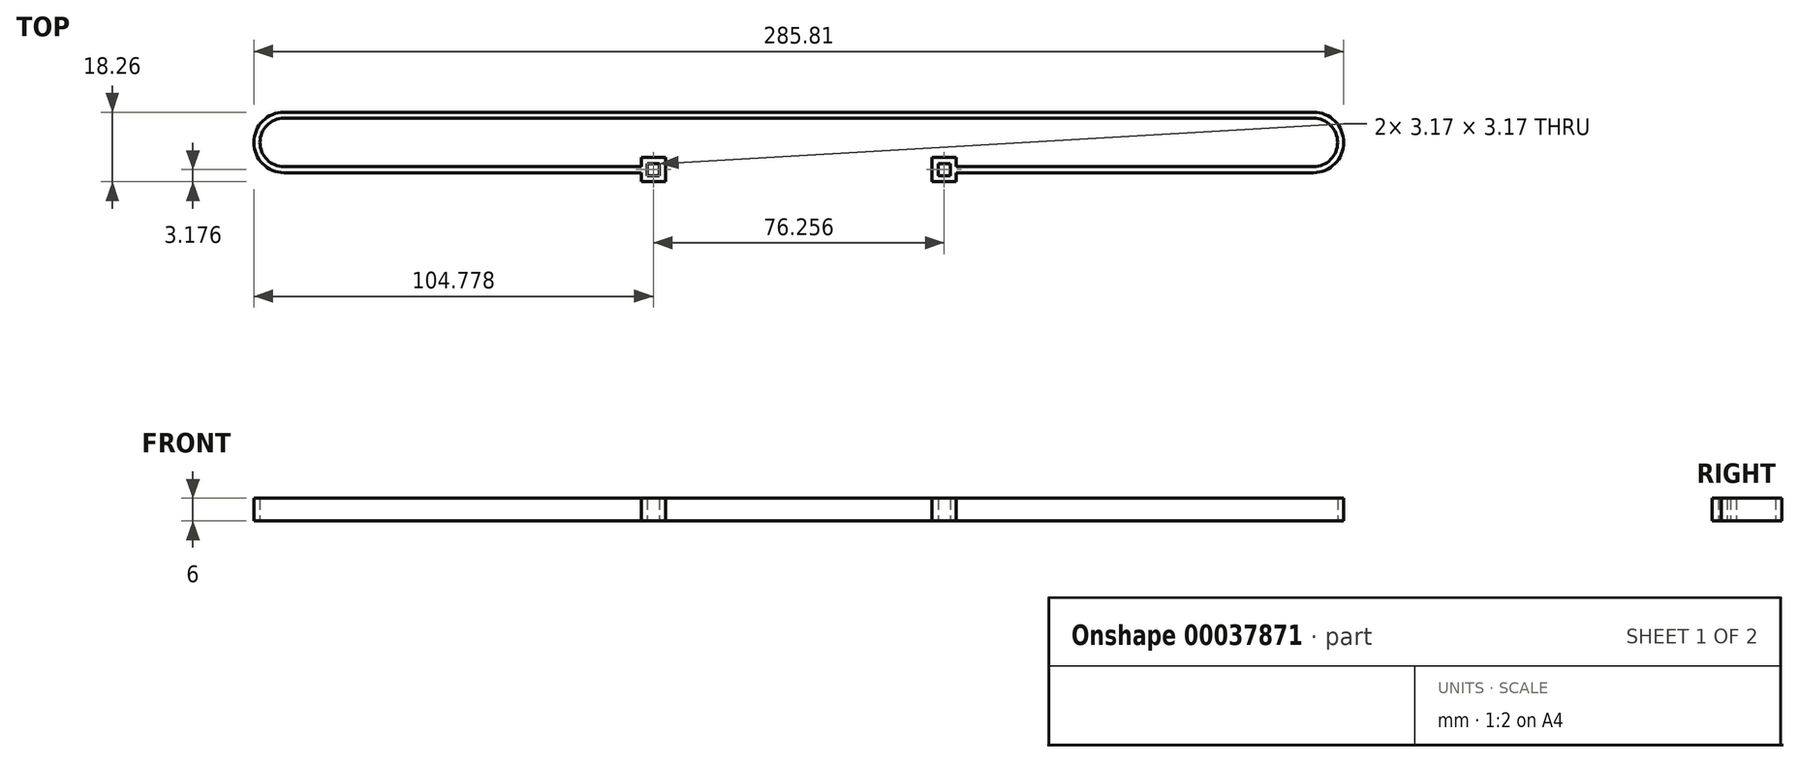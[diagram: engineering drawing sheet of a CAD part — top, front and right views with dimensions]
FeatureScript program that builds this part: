
annotation { "Feature Type Name" : "Feature", "Feature Type Description" : "" }
export const myFeature = defineFeature(function(context is Context, id is Id, definition is map)
    precondition{}
    {
        {
            var Q0;
            Q0=qCreatedBy(makeId("Top.planeOp"),FACE);
            var sketch = newSketch(context, id + "F0", { "sketchPlane" : qUnion([Q0])});
            skLineSegment(sketch, "E0", {"start": v(-672, -278.67) * mm, "end": v(-672, -277.09) * mm, "construction": true});
            skLineSegment(sketch, "E1", {"start": v(-824.4, -300.67) * mm, "end": v(-824.4, -302.26) * mm, "construction": true});
            skLineSegment(sketch, "E2", {"start": v(-763.7, -278.67) * mm, "end": v(-763.7, -277.09) * mm, "construction": true});
            skLineSegment(sketch, "E3", {"start": v(269.93, 7.94) * mm, "end": v(0, 7.94) * mm});
            skLineSegment(sketch, "E4", {"start": v(269.93, 6.35) * mm, "end": v(0, 6.35) * mm});
            skLineSegment(sketch, "E5", {"start": v(0, 6.35) * mm, "end": v(0, -6.35) * mm, "construction": true});
            skLineSegment(sketch, "E6", {"start": v(269.93, 6.35) * mm, "end": v(269.93, -6.35) * mm, "construction": true});
            skArc(sketch, "E7", {"start": v(0, 6.35) * mm, "mid": v(-6.35, 0) * mm, "end": v(0, -6.35) * mm});
            skArc(sketch, "E8", {"start": v(0, 7.94) * mm, "mid": v(-7.94, 0) * mm, "end": v(0, -7.94) * mm});
            skLineSegment(sketch, "E9", {"start": v(0, -6.35) * mm, "end": v(93.66, -6.35) * mm});
            skLineSegment(sketch, "E10", {"start": v(93.66, -6.35) * mm, "end": v(93.66, -3.97) * mm});
            skLineSegment(sketch, "E11", {"start": v(93.66, -3.97) * mm, "end": v(100.01, -3.97) * mm});
            skLineSegment(sketch, "E12", {"start": v(100.01, -3.97) * mm, "end": v(100.01, -10.32) * mm});
            skLineSegment(sketch, "E13", {"start": v(0, -7.94) * mm, "end": v(93.66, -7.94) * mm});
            skLineSegment(sketch, "E14.bottom", {"start": v(95.25, -8.73) * mm, "end": v(98.43, -8.73) * mm});
            skLineSegment(sketch, "E14.top", {"start": v(95.25, -5.56) * mm, "end": v(98.43, -5.56) * mm});
            skLineSegment(sketch, "E14.left", {"start": v(95.25, -8.73) * mm, "end": v(95.25, -5.56) * mm});
            skLineSegment(sketch, "E14.right", {"start": v(98.43, -8.73) * mm, "end": v(98.43, -5.56) * mm});
            skLineSegment(sketch, "E15", {"start": v(96.84, -5.56) * mm, "end": v(96.84, -3.97) * mm, "construction": true});
            skArc(sketch, "E16", {"start": v(269.93, -6.35) * mm, "mid": v(276.28, 0) * mm, "end": v(269.93, 6.35) * mm});
            skArc(sketch, "E17", {"start": v(269.93, -7.94) * mm, "mid": v(277.87, 0) * mm, "end": v(269.93, 7.94) * mm});
            skLineSegment(sketch, "E18", {"start": v(269.93, -6.35) * mm, "end": v(176.27, -6.35) * mm});
            skLineSegment(sketch, "E19", {"start": v(269.93, -7.94) * mm, "end": v(176.27, -7.94) * mm});
            skLineSegment(sketch, "E20.bottom", {"start": v(171.5, -5.56) * mm, "end": v(174.68, -5.56) * mm});
            skLineSegment(sketch, "E20.top", {"start": v(171.5, -8.73) * mm, "end": v(174.68, -8.73) * mm});
            skLineSegment(sketch, "E20.left", {"start": v(171.5, -5.56) * mm, "end": v(171.5, -8.73) * mm});
            skLineSegment(sketch, "E20.right", {"start": v(174.68, -5.56) * mm, "end": v(174.68, -8.73) * mm});
            skLineSegment(sketch, "E21", {"start": v(173.1, -5.56) * mm, "end": v(173.1, -3.97) * mm});
            skLineSegment(sketch, "E22", {"start": v(169.92, -10.32) * mm, "end": v(169.92, -3.97) * mm});
            skLineSegment(sketch, "E23", {"start": v(169.92, -3.97) * mm, "end": v(176.27, -3.97) * mm});
            skLineSegment(sketch, "E24", {"start": v(176.27, -3.97) * mm, "end": v(176.27, -6.35) * mm});
            skLineSegment(sketch, "E25", {"start": v(98.43, -7.14) * mm, "end": v(100.01, -7.14) * mm, "construction": true});
            skPoint(sketch, "E25.endSnap0", {"position": v(98.43, -7.14) * mm});
            skLineSegment(sketch, "E26", {"start": v(171.5, -7.14) * mm, "end": v(169.92, -7.14) * mm, "construction": true});
            skPoint(sketch, "E26.endSnap0", {"position": v(171.5, -7.14) * mm});
            skLineSegment(sketch, "E27", {"start": v(100.01, -10.32) * mm, "end": v(93.66, -10.32) * mm});
            skLineSegment(sketch, "E28", {"start": v(93.66, -10.32) * mm, "end": v(93.66, -7.94) * mm});
            skLineSegment(sketch, "E29", {"start": v(169.92, -10.32) * mm, "end": v(176.27, -10.32) * mm});
            skLineSegment(sketch, "E30", {"start": v(176.27, -10.32) * mm, "end": v(176.27, -7.94) * mm});
            skLineSegment(sketch, "E31", {"start": v(269.93, -7.94) * mm, "end": v(269.93, -6.35) * mm, "construction": true});
            skSolve(sketch);
        }
        {
            var Q0;
            Q0=qSketchRegion(id+"F0",true);
            extrude(context, id + "F1", {"entities" : qUnion([Q0]), "depth" : 6 * mm});
        }
    });
